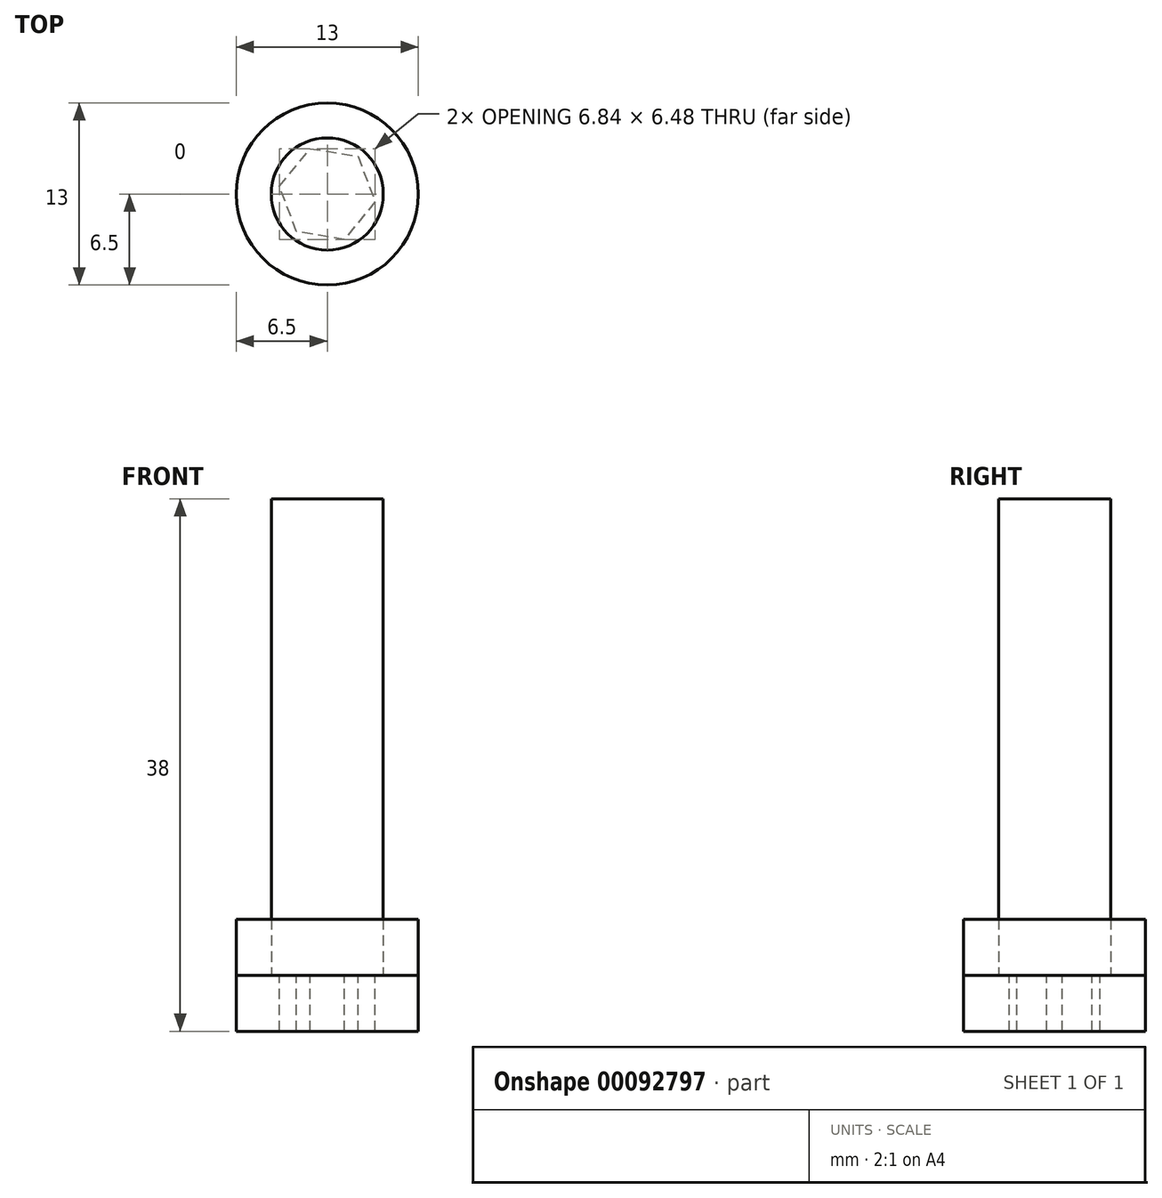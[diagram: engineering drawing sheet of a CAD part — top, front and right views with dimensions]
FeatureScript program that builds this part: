
annotation { "Feature Type Name" : "Feature", "Feature Type Description" : "" }
export const myFeature = defineFeature(function(context is Context, id is Id, definition is map)
    precondition{}
    {
        {
            var Q0;
            Q0=qCreatedBy(makeId("Top.planeOp"),FACE);
            var sketch = newSketch(context, id + "F0", { "sketchPlane" : qUnion([Q0])});
            skCircle(sketch, "E0", {"center": v(0, 0) * mm, "radius": 6.5 * mm});
            skCircle(sketch, "E1", {"center": v(0, 0) * mm, "radius": 4 * mm});
            skCircle(sketch, "E2.cCircle", {"center": v(0, 0) * mm, "radius": 3.46 * mm, "construction": true});
            skLineSegment(sketch, "E2.0", {"start": v(1.23, -3.24) * mm, "end": v(-2.2, -2.68) * mm});
            skLineSegment(sketch, "E2.1", {"start": v(-2.2, -2.68) * mm, "end": v(-3.42, 0.56) * mm});
            skLineSegment(sketch, "E2.2", {"start": v(-3.42, 0.56) * mm, "end": v(-1.23, 3.24) * mm});
            skLineSegment(sketch, "E2.3", {"start": v(-1.23, 3.24) * mm, "end": v(2.2, 2.68) * mm});
            skLineSegment(sketch, "E2.4", {"start": v(2.2, 2.68) * mm, "end": v(3.42, -0.56) * mm});
            skLineSegment(sketch, "E2.5", {"start": v(3.42, -0.56) * mm, "end": v(1.23, -3.24) * mm});
            skSolve(sketch);
        }
        {
            var Q0;
            Q0=makeQuery(id+"F0.imprint","IMPRINT",FACE,{"disambiguationData":[TD([[makeQuery(id+"F0.imprint","IMPRINT",EDGE,{"derivedFrom":sQuery(id+"F0.wireOp",EDGE,"E1")}),1.0]])]});
            var Q1;
            Q1=makeQuery(id+"F0.imprint","IMPRINT",FACE,{"disambiguationData":[TD([[makeQuery(id+"F0.imprint","IMPRINT",EDGE,{"derivedFrom":sQuery(id+"F0.wireOp",EDGE,"E2.0")}),-1.0]])]});
            extrude(context, id + "F1", {"entities" : qUnion([Q0, Q1]), "depth" : 34 * mm});
        }
        {
            var Q0;
            Q0=makeQuery(id+"F0.imprint","IMPRINT",FACE,{"disambiguationData":[TD([[makeQuery(id+"F0.imprint","IMPRINT",EDGE,{"derivedFrom":sQuery(id+"F0.wireOp",EDGE,"E1")}),1.0]])]});
            var Q1;
            Q1=makeQuery(id+"F0.imprint","IMPRINT",FACE,{"disambiguationData":[TD([[makeQuery(id+"F0.imprint","IMPRINT",EDGE,{"derivedFrom":sQuery(id+"F0.wireOp",EDGE,"E0")}),1.0]])]});
            extrude(context, id + "F2", {"entities" : qUnion([Q0, Q1]), "endBound" : BoundingType.SYMMETRIC, "depth" : 8 * mm});
        }
        {
            var Q0;
            Q0=makeQuery(id+"F0.imprint","IMPRINT",FACE,{"disambiguationData":[TD([[makeQuery(id+"F0.imprint","IMPRINT",EDGE,{"derivedFrom":sQuery(id+"F0.wireOp",EDGE,"E1")}),1.0]])]});
            var Q1;
            Q1=makeQuery(id+"F0.imprint","IMPRINT",FACE,{"disambiguationData":[TD([[makeQuery(id+"F0.imprint","IMPRINT",EDGE,{"derivedFrom":sQuery(id+"F0.wireOp",EDGE,"E0")}),1.0]])]});
            extrude(context, id + "F3", {"entities" : qUnion([Q0, Q1]), "oppositeDirection" : true, "depth" : 4 * mm});
        }
    });
